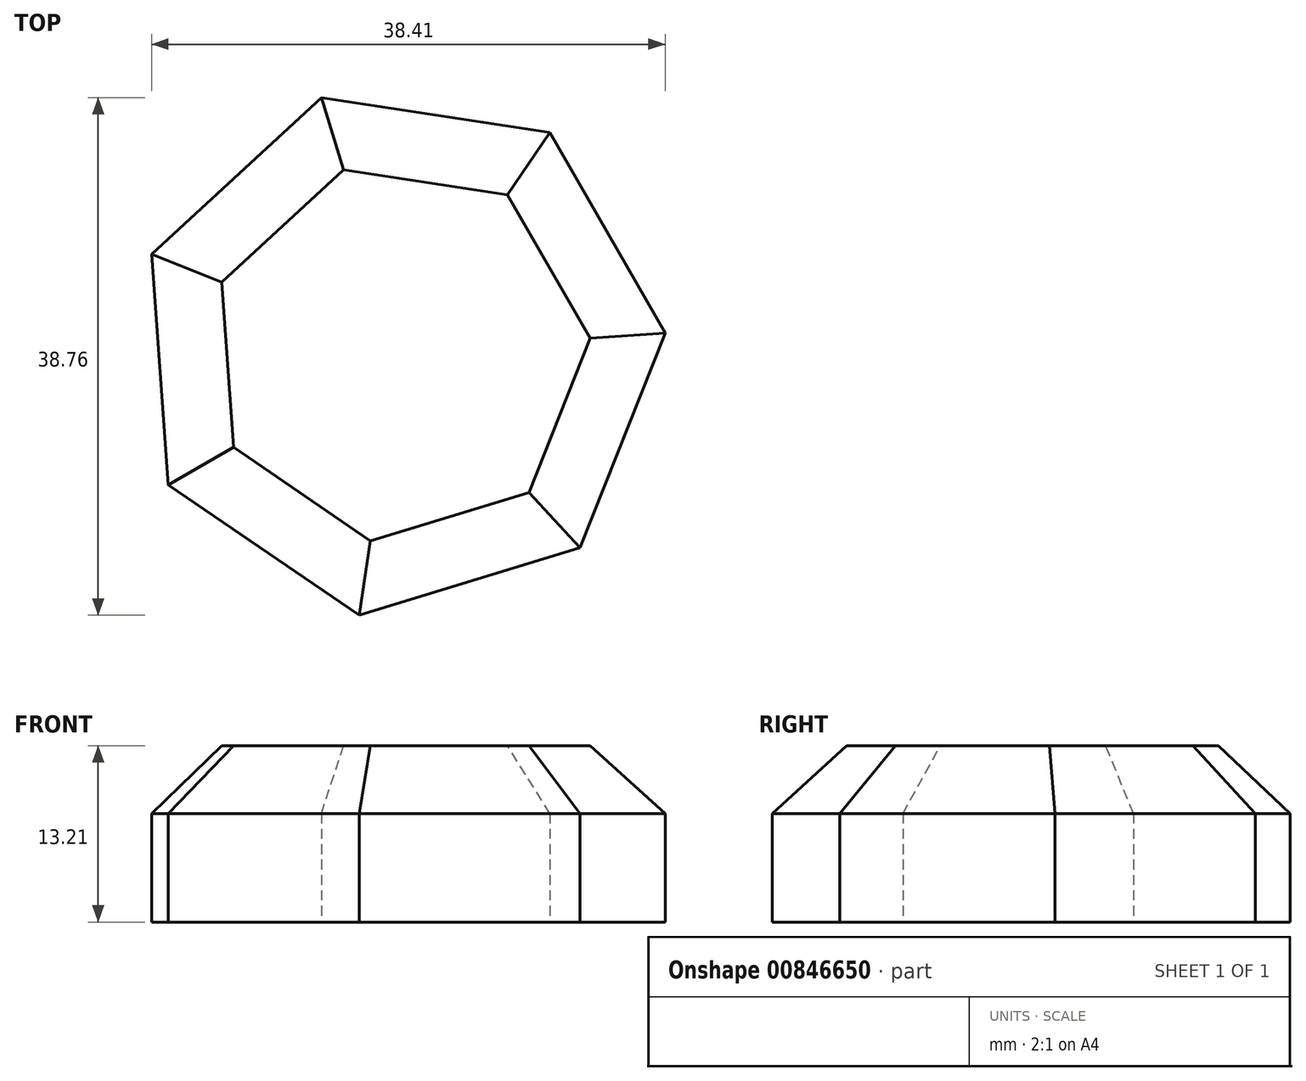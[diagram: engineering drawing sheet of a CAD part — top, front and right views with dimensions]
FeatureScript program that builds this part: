
annotation { "Feature Type Name" : "Feature", "Feature Type Description" : "" }
export const myFeature = defineFeature(function(context is Context, id is Id, definition is map)
    precondition{}
    {
        {
            var Q0;
            Q0=qCreatedBy(makeId("Top.planeOp"),FACE);
            var sketch = newSketch(context, id + "F0", { "sketchPlane" : qUnion([Q0])});
            skCircle(sketch, "E0.cCircle", {"center": v(0, 0) * mm, "radius": 17.96 * mm, "construction": true});
            skLineSegment(sketch, "E0.0", {"start": v(11.26, 16.44) * mm, "end": v(19.88, 1.44) * mm});
            skLineSegment(sketch, "E0.1", {"start": v(19.88, 1.44) * mm, "end": v(13.52, -14.64) * mm});
            skLineSegment(sketch, "E0.2", {"start": v(13.52, -14.64) * mm, "end": v(-3.02, -19.7) * mm});
            skLineSegment(sketch, "E0.3", {"start": v(-3.02, -19.7) * mm, "end": v(-17.28, -9.92) * mm});
            skLineSegment(sketch, "E0.4", {"start": v(-17.28, -9.92) * mm, "end": v(-18.53, 7.32) * mm});
            skLineSegment(sketch, "E0.5", {"start": v(-18.53, 7.32) * mm, "end": v(-5.83, 19.06) * mm});
            skLineSegment(sketch, "E0.6", {"start": v(-5.83, 19.06) * mm, "end": v(11.26, 16.44) * mm});
            skPoint(sketch, "E0.0.midPoint", {"position": v(15.57, 8.94) * mm});
            skSolve(sketch);
        }
        {
            var Q0;
            Q0=makeQuery(id+"F0.imprint","IMPRINT",FACE,{"disambiguationData":[TD([[makeQuery(id+"F0.imprint","IMPRINT",EDGE,{"derivedFrom":sQuery(id+"F0.wireOp",EDGE,"E0.0")}),-1.0]])]});
            extrude(context, id + "F1", {"entities" : qUnion([Q0]), "depth" : 13.2 * mm, "offsetDistance" : 25.4 * mm});
        }
        {
            var Q0;
            Q0=makeQuery(id+"F1.opExtrude","CAP_FACE",FACE,{"disambiguationData":[OSD([sQuery(id+"F0.wireOp",EDGE,"E0.0"),sQuery(id+"F0.wireOp",EDGE,"E0.1"),sQuery(id+"F0.wireOp",EDGE,"E0.2"),sQuery(id+"F0.wireOp",EDGE,"E0.3"),sQuery(id+"F0.wireOp",EDGE,"E0.4"),sQuery(id+"F0.wireOp",EDGE,"E0.5"),sQuery(id+"F0.wireOp",EDGE,"E0.6")])],"isStart":false});
            chamfer(context, id + "F2", {"entities" : qUnion([Q0]), "width" : 5.08 * mm, "tangentPropagation" : true});
        }
    });
